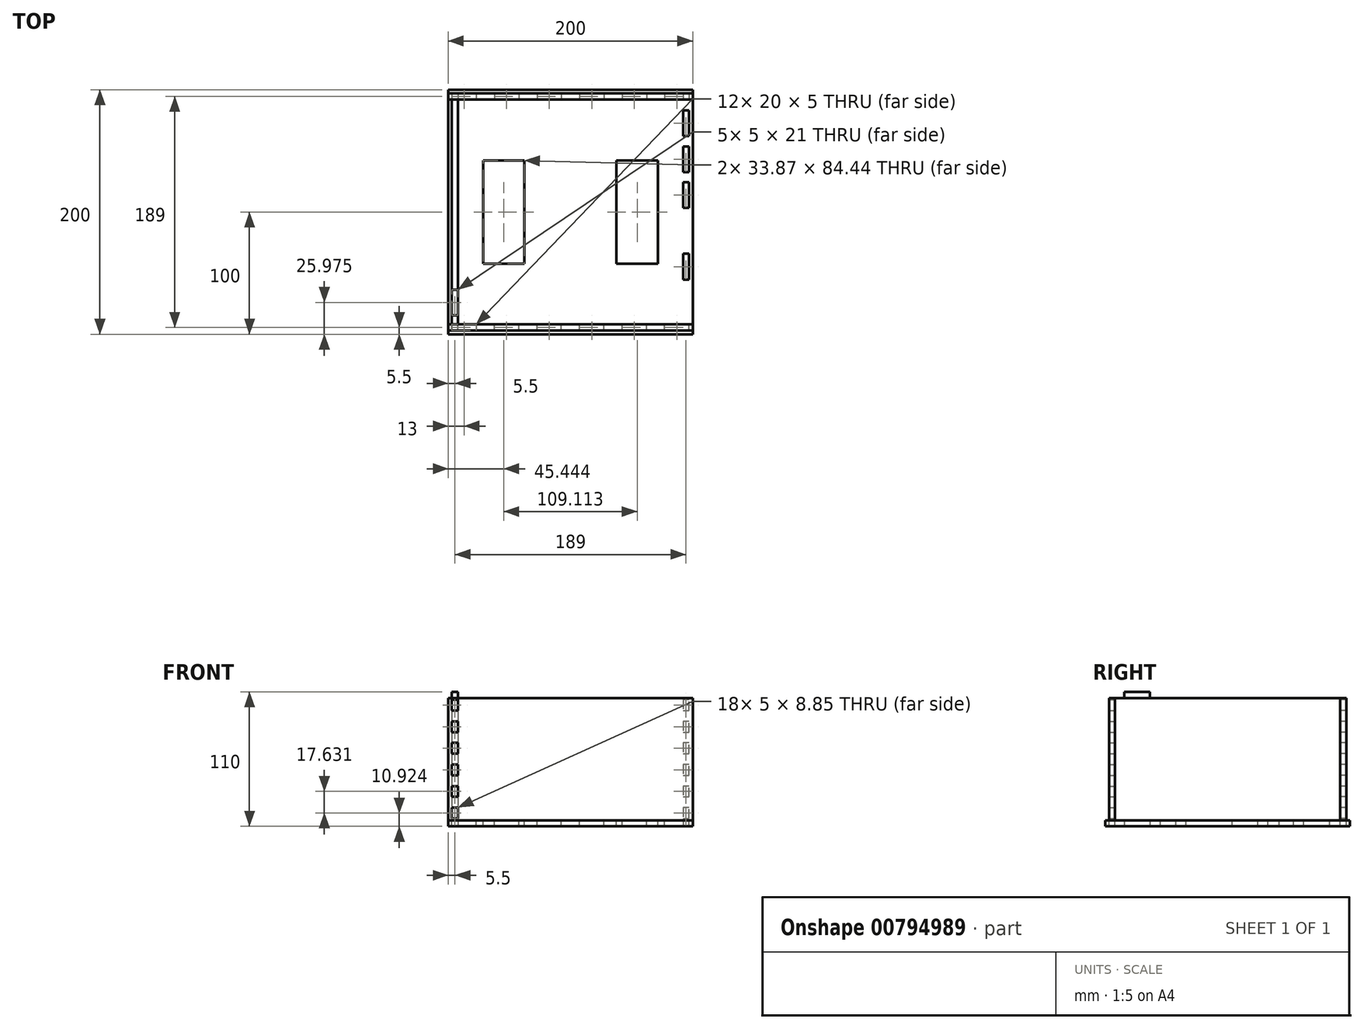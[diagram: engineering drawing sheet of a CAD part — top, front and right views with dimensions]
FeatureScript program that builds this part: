
annotation { "Feature Type Name" : "Feature", "Feature Type Description" : "" }
export const myFeature = defineFeature(function(context is Context, id is Id, definition is map)
    precondition{}
    {
        {
            assignVariable(context, id + "F0", {"name" : "width", "anyValue" : 5});
        }
        {
            var Q0;
            Q0=qCreatedBy(makeId("Top.planeOp"),FACE);
            var sketch = newSketch(context, id + "F1", { "sketchPlane" : qUnion([Q0])});
            skLineSegment(sketch, "E0.bottom", {"start": v(100, -100) * mm, "end": v(-100, -100) * mm});
            skLineSegment(sketch, "E0.top", {"start": v(100, 100) * mm, "end": v(-100, 100) * mm});
            skLineSegment(sketch, "E0.left", {"start": v(100, -100) * mm, "end": v(100, 100) * mm});
            skLineSegment(sketch, "E0.right", {"start": v(-100, -100) * mm, "end": v(-100, 100) * mm});
            skPoint(sketch, "E0.middle", {"position": v(0, 0) * mm});
            skLineSegment(sketch, "E1.0", {"start": v(97, 97) * mm, "end": v(-97, 97) * mm, "construction": true});
            skLineSegment(sketch, "E1.1", {"start": v(97, -97) * mm, "end": v(97, 97) * mm, "construction": true});
            skLineSegment(sketch, "E1.2", {"start": v(97, -97) * mm, "end": v(-97, -97) * mm, "construction": true});
            skLineSegment(sketch, "E1.3", {"start": v(-97, -97) * mm, "end": v(-97, 97) * mm, "construction": true});
            skSolve(sketch);
        }
        {
            var Q0;
            Q0=qSketchRegion(id+"F1",true);
            extrude(context, id + "F2", {"entities" : qUnion([Q0]), "depth" : (getVariable(context, 'width')) * mm});
        }
        {
            var Q0;
            Q0=makeQuery(id+"F2.opExtrude","CAP_FACE",FACE,{"disambiguationData":[OSD([sQuery(id+"F1.wireOp",EDGE,"E0.bottom"),sQuery(id+"F1.wireOp",EDGE,"E0.top"),sQuery(id+"F1.wireOp",EDGE,"E0.left"),sQuery(id+"F1.wireOp",EDGE,"E0.right")])],"isStart":false});
            var sketch = newSketch(context, id + "F3", { "sketchPlane" : qUnion([Q0])});
            skLineSegment(sketch, "E2.0", {"start": v(97, 97) * mm, "end": v(-97, 97) * mm, "construction": true});
            skLineSegment(sketch, "E2.1", {"start": v(97, -97) * mm, "end": v(97, 97) * mm, "construction": true});
            skLineSegment(sketch, "E2.2", {"start": v(97, -97) * mm, "end": v(-97, -97) * mm, "construction": true});
            skLineSegment(sketch, "E2.3", {"start": v(-97, -97) * mm, "end": v(-97, 97) * mm, "construction": true});
            skLineSegment(sketch, "E3.bottom", {"start": v(-97, 97) * mm, "end": v(-77, 97) * mm, "construction": true});
            skLineSegment(sketch, "E3.left", {"start": v(-97, 97) * mm, "end": v(-97, 92) * mm, "construction": true});
            skLineSegment(sketch, "E4.bottom", {"start": v(-97, 97) * mm, "end": v(-77, 97) * mm});
            skLineSegment(sketch, "E4.top", {"start": v(-97, 92) * mm, "end": v(-77, 92) * mm});
            skLineSegment(sketch, "E4.left", {"start": v(-97, 97) * mm, "end": v(-97, 92) * mm});
            skLineSegment(sketch, "E4.right", {"start": v(-77, 97) * mm, "end": v(-77, 92) * mm});
            skLineSegment(sketch, "E5.1.0.0", {"start": v(-42.2, 97) * mm, "end": v(-42.2, 92) * mm});
            skLineSegment(sketch, "E5.1.0.1", {"start": v(-62.2, 92) * mm, "end": v(-42.2, 92) * mm});
            skLineSegment(sketch, "E5.1.0.2", {"start": v(-62.2, 97) * mm, "end": v(-42.2, 97) * mm});
            skLineSegment(sketch, "E5.1.0.3", {"start": v(-62.2, 97) * mm, "end": v(-62.2, 92) * mm});
            skLineSegment(sketch, "E5.2.0.0", {"start": v(-7.4, 97) * mm, "end": v(-7.4, 92) * mm});
            skLineSegment(sketch, "E5.2.0.1", {"start": v(-27.4, 92) * mm, "end": v(-7.4, 92) * mm});
            skLineSegment(sketch, "E5.2.0.2", {"start": v(-27.4, 97) * mm, "end": v(-7.4, 97) * mm});
            skLineSegment(sketch, "E5.2.0.3", {"start": v(-27.4, 97) * mm, "end": v(-27.4, 92) * mm});
            skLineSegment(sketch, "E5.3.0.0", {"start": v(27.4, 97) * mm, "end": v(27.4, 92) * mm});
            skLineSegment(sketch, "E5.3.0.1", {"start": v(7.4, 92) * mm, "end": v(27.4, 92) * mm});
            skLineSegment(sketch, "E5.3.0.2", {"start": v(7.4, 97) * mm, "end": v(27.4, 97) * mm});
            skLineSegment(sketch, "E5.3.0.3", {"start": v(7.4, 97) * mm, "end": v(7.4, 92) * mm});
            skLineSegment(sketch, "E5.4.0.0", {"start": v(62.2, 97) * mm, "end": v(62.2, 92) * mm});
            skLineSegment(sketch, "E5.4.0.1", {"start": v(42.2, 92) * mm, "end": v(62.2, 92) * mm});
            skLineSegment(sketch, "E5.4.0.2", {"start": v(42.2, 97) * mm, "end": v(62.2, 97) * mm});
            skLineSegment(sketch, "E5.4.0.3", {"start": v(42.2, 97) * mm, "end": v(42.2, 92) * mm});
            skLineSegment(sketch, "E5.5.0.0", {"start": v(97, 97) * mm, "end": v(97, 92) * mm});
            skLineSegment(sketch, "E5.5.0.1", {"start": v(77, 92) * mm, "end": v(97, 92) * mm});
            skLineSegment(sketch, "E5.5.0.2", {"start": v(77, 97) * mm, "end": v(97, 97) * mm});
            skLineSegment(sketch, "E5.5.0.3", {"start": v(77, 97) * mm, "end": v(77, 92) * mm});
            skLineSegment(sketch, "E5.direction1", {"start": v(-77, 92) * mm, "end": v(-42.2, 92) * mm, "construction": true});
            skLineSegment(sketch, "E6.MirrorCS", {"start": v(-97, -97) * mm, "end": v(-97, -92) * mm});
            skLineSegment(sketch, "E7.MirrorCS", {"start": v(-77, -97) * mm, "end": v(-77, -92) * mm});
            skLineSegment(sketch, "E8.MirrorCS", {"start": v(-97, -97) * mm, "end": v(-97, -92) * mm, "construction": true});
            skLineSegment(sketch, "E9.MirrorCS", {"start": v(97, -97) * mm, "end": v(97, -92) * mm});
            skLineSegment(sketch, "E10.MirrorCS", {"start": v(77, -97) * mm, "end": v(77, -92) * mm});
            skLineSegment(sketch, "E11.MirrorCS", {"start": v(-42.2, -97) * mm, "end": v(-42.2, -92) * mm});
            skLineSegment(sketch, "E12.MirrorCS", {"start": v(62.2, -97) * mm, "end": v(62.2, -92) * mm});
            skLineSegment(sketch, "E13.MirrorCS", {"start": v(-62.2, -97) * mm, "end": v(-62.2, -92) * mm});
            skLineSegment(sketch, "E14.MirrorCS", {"start": v(-7.4, -97) * mm, "end": v(-7.4, -92) * mm});
            skLineSegment(sketch, "E15.MirrorCS", {"start": v(-27.4, -97) * mm, "end": v(-27.4, -92) * mm});
            skLineSegment(sketch, "E16.MirrorCS", {"start": v(7.4, -97) * mm, "end": v(7.4, -92) * mm});
            skLineSegment(sketch, "E17.MirrorCS", {"start": v(27.4, -97) * mm, "end": v(27.4, -92) * mm});
            skLineSegment(sketch, "E18.MirrorCS", {"start": v(42.2, -97) * mm, "end": v(42.2, -92) * mm});
            skLineSegment(sketch, "E19.MirrorCS", {"start": v(-62.2, -92) * mm, "end": v(-42.2, -92) * mm});
            skLineSegment(sketch, "E20.MirrorCS", {"start": v(-27.4, -97) * mm, "end": v(-7.4, -97) * mm});
            skLineSegment(sketch, "E21.MirrorCS", {"start": v(7.4, -97) * mm, "end": v(27.4, -97) * mm});
            skLineSegment(sketch, "E22.MirrorCS", {"start": v(42.2, -97) * mm, "end": v(62.2, -97) * mm});
            skLineSegment(sketch, "E23.MirrorCS", {"start": v(77, -97) * mm, "end": v(97, -97) * mm});
            skLineSegment(sketch, "E24.MirrorCS", {"start": v(-62.2, -97) * mm, "end": v(-42.2, -97) * mm});
            skLineSegment(sketch, "E25.MirrorCS", {"start": v(-97, -97) * mm, "end": v(-77, -97) * mm});
            skLineSegment(sketch, "E26.MirrorCS", {"start": v(42.2, -92) * mm, "end": v(62.2, -92) * mm});
            skLineSegment(sketch, "E27.MirrorCS", {"start": v(77, -92) * mm, "end": v(97, -92) * mm});
            skLineSegment(sketch, "E28.MirrorCS", {"start": v(-77, -92) * mm, "end": v(-42.2, -92) * mm, "construction": true});
            skLineSegment(sketch, "E29.MirrorCS", {"start": v(-27.4, -92) * mm, "end": v(-7.4, -92) * mm});
            skLineSegment(sketch, "E30.MirrorCS", {"start": v(-97, -97) * mm, "end": v(-77, -97) * mm, "construction": true});
            skLineSegment(sketch, "E31.MirrorCS", {"start": v(-97, -92) * mm, "end": v(-77, -92) * mm});
            skLineSegment(sketch, "E32.MirrorCS", {"start": v(7.4, -92) * mm, "end": v(27.4, -92) * mm});
            skSolve(sketch);
        }
        {
            var Q0;
            Q0=qSketchRegion(id+"F3",true);
            extrude(context, id + "F4", {"entities" : qUnion([Q0]), "operationType" : NewBodyOperationType.REMOVE, "oppositeDirection" : true, "depth" : 25 * mm});
        }
        {
            var Q0;
            Q0=makeQuery(id+"F2.opExtrude","CAP_FACE",FACE,{"disambiguationData":[OSD([sQuery(id+"F1.wireOp",EDGE,"E0.bottom"),sQuery(id+"F1.wireOp",EDGE,"E0.top"),sQuery(id+"F1.wireOp",EDGE,"E0.left"),sQuery(id+"F1.wireOp",EDGE,"E0.right")])],"isStart":false});
            var sketch = newSketch(context, id + "F5", { "sketchPlane" : qUnion([Q0])});
            skLineSegment(sketch, "E33.0", {"start": v(-97, 97) * mm, "end": v(-77, 97) * mm});
            skSolve(sketch);
        }
        {
            var Q0;
            Q0=makeQuery(id+"F5.imprint","IMPRINT",FACE,{"disambiguationData":[TD([[makeQuery(id+"F5.imprint","IMPRINT",EDGE,{"derivedFrom":makeQuery(id+"F4.boolean.opBoolean","COPY",EDGE,{"derivedFrom":makeQuery(id+"F4.opExtrude","CAP_EDGE",EDGE,{"disambiguationData":[OSD([sQuery(id+"F3.wireOp",EDGE,"E5.1.0.0")])],"isStart":true})})}),-1.0]])]});
            var Q1;
            Q1=makeQuery(id+"F5.imprint","IMPRINT",FACE,{"disambiguationData":[TD([[makeQuery(id+"F5.imprint","IMPRINT",EDGE,{"derivedFrom":sQuery(id+"F5.wireOp",EDGE,"E33.0")}),-1.0]])]});
            var Q2;
            Q2=makeQuery(id+"F5.imprint","IMPRINT",FACE,{"disambiguationData":[TD([[makeQuery(id+"F5.imprint","IMPRINT",EDGE,{"derivedFrom":makeQuery(id+"F4.boolean.opBoolean","COPY",EDGE,{"derivedFrom":makeQuery(id+"F4.opExtrude","CAP_EDGE",EDGE,{"disambiguationData":[OSD([sQuery(id+"F3.wireOp",EDGE,"E5.2.0.0")])],"isStart":true})})}),-1.0]])]});
            var Q3;
            Q3=makeQuery(id+"F5.imprint","IMPRINT",FACE,{"disambiguationData":[TD([[makeQuery(id+"F5.imprint","IMPRINT",EDGE,{"derivedFrom":makeQuery(id+"F4.boolean.opBoolean","COPY",EDGE,{"derivedFrom":makeQuery(id+"F4.opExtrude","CAP_EDGE",EDGE,{"disambiguationData":[OSD([sQuery(id+"F3.wireOp",EDGE,"E5.3.0.0")])],"isStart":true})})}),-1.0]])]});
            var Q4;
            Q4=makeQuery(id+"F5.imprint","IMPRINT",FACE,{"disambiguationData":[TD([[makeQuery(id+"F5.imprint","IMPRINT",EDGE,{"derivedFrom":makeQuery(id+"F4.boolean.opBoolean","COPY",EDGE,{"derivedFrom":makeQuery(id+"F4.opExtrude","CAP_EDGE",EDGE,{"disambiguationData":[OSD([sQuery(id+"F3.wireOp",EDGE,"E5.4.0.0")])],"isStart":true})})}),-1.0]])]});
            var Q5;
            Q5=makeQuery(id+"F5.imprint","IMPRINT",FACE,{"disambiguationData":[TD([[makeQuery(id+"F5.imprint","IMPRINT",EDGE,{"derivedFrom":makeQuery(id+"F4.boolean.opBoolean","COPY",EDGE,{"derivedFrom":makeQuery(id+"F4.opExtrude","CAP_EDGE",EDGE,{"disambiguationData":[OSD([sQuery(id+"F3.wireOp",EDGE,"E5.5.0.0")])],"isStart":true})})}),-1.0]])]});
            var Q6;
            Q6=makeQuery(id+"F2.opExtrude","CAP_FACE",FACE,{"disambiguationData":[OSD([sQuery(id+"F1.wireOp",EDGE,"E0.bottom"),sQuery(id+"F1.wireOp",EDGE,"E0.top"),sQuery(id+"F1.wireOp",EDGE,"E0.left"),sQuery(id+"F1.wireOp",EDGE,"E0.right")])],"isStart":true});
            extrude(context, id + "F6", {"entities" : qUnion([Q0, Q1, Q2, Q3, Q4, Q5]), "endBound" : BoundingType.UP_TO_SURFACE, "oppositeDirection" : true, "endBoundEntityFace" : qUnion([Q6]), "depth" : 25 * mm});
        }
        {
            var Q0;
            Q0=makeQuery(id+"F2.opExtrude","CAP_FACE",FACE,{"disambiguationData":[OSD([sQuery(id+"F1.wireOp",EDGE,"E0.bottom"),sQuery(id+"F1.wireOp",EDGE,"E0.top"),sQuery(id+"F1.wireOp",EDGE,"E0.left"),sQuery(id+"F1.wireOp",EDGE,"E0.right")])],"isStart":false});
            var sketch = newSketch(context, id + "F7", { "sketchPlane" : qUnion([Q0])});
            skLineSegment(sketch, "E34.bottom", {"start": v(-100, 97) * mm, "end": v(100, 97) * mm});
            skLineSegment(sketch, "E34.top", {"start": v(-100, 92) * mm, "end": v(100, 92) * mm});
            skLineSegment(sketch, "E34.left", {"start": v(-100, 97) * mm, "end": v(-100, 92) * mm});
            skLineSegment(sketch, "E34.right", {"start": v(100, 97) * mm, "end": v(100, 92) * mm});
            skSolve(sketch);
        }
        {
            var Q0;
            Q0=qSketchRegion(id+"F7",true);
            extrude(context, id + "F8", {"entities" : qUnion([Q0]), "depth" : 100 * mm});
        }
        {
            var Q0;
            Q0=makeQuery(id+"F2.opExtrude","CAP_FACE",FACE,{"disambiguationData":[OSD([sQuery(id+"F1.wireOp",EDGE,"E0.bottom"),sQuery(id+"F1.wireOp",EDGE,"E0.top"),sQuery(id+"F1.wireOp",EDGE,"E0.left"),sQuery(id+"F1.wireOp",EDGE,"E0.right")])],"isStart":true});
            var sketch = newSketch(context, id + "F9", { "sketchPlane" : qUnion([Q0])});
            skLineSegment(sketch, "E35.0", {"start": v(97, 97) * mm, "end": v(97, -97) * mm});
            skLineSegment(sketch, "E35.1", {"start": v(97, 97) * mm, "end": v(-97, 97) * mm});
            skLineSegment(sketch, "E35.2", {"start": v(-97, 97) * mm, "end": v(-97, -97) * mm});
            skLineSegment(sketch, "E35.3", {"start": v(97, -97) * mm, "end": v(-97, -97) * mm});
            skLineSegment(sketch, "E36.bottom", {"start": v(-97, 84.52) * mm, "end": v(-92, 84.52) * mm});
            skLineSegment(sketch, "E36.top", {"start": v(-97, 63.52) * mm, "end": v(-92, 63.52) * mm});
            skLineSegment(sketch, "E36.left", {"start": v(-97, 84.52) * mm, "end": v(-97, 63.52) * mm});
            skLineSegment(sketch, "E36.right", {"start": v(-92, 84.52) * mm, "end": v(-92, 63.52) * mm});
            skLineSegment(sketch, "E37.1.0.0", {"start": v(-97, 55.22) * mm, "end": v(-97, 34.22) * mm});
            skLineSegment(sketch, "E37.1.0.1", {"start": v(-97, 55.22) * mm, "end": v(-92, 55.22) * mm});
            skLineSegment(sketch, "E37.1.0.2", {"start": v(-97, 34.22) * mm, "end": v(-92, 34.22) * mm});
            skLineSegment(sketch, "E37.1.0.3", {"start": v(-92, 55.22) * mm, "end": v(-92, 34.22) * mm});
            skLineSegment(sketch, "E37.2.0.0", {"start": v(-97, 25.91) * mm, "end": v(-97, 4.91) * mm});
            skLineSegment(sketch, "E37.2.0.1", {"start": v(-97, 25.91) * mm, "end": v(-92, 25.91) * mm});
            skLineSegment(sketch, "E37.2.0.2", {"start": v(-97, 4.91) * mm, "end": v(-92, 4.91) * mm});
            skLineSegment(sketch, "E37.2.0.3", {"start": v(-92, 25.91) * mm, "end": v(-92, 4.91) * mm});
            skLineSegment(sketch, "E37.3.0.0", {"start": v(-97, -3.4) * mm, "end": v(-97, -24.4) * mm});
            skLineSegment(sketch, "E37.3.0.1", {"start": v(-97, -3.4) * mm, "end": v(-92, -3.4) * mm});
            skLineSegment(sketch, "E37.3.0.2", {"start": v(-97, -24.4) * mm, "end": v(-92, -24.4) * mm});
            skLineSegment(sketch, "E37.3.0.3", {"start": v(-92, -3.4) * mm, "end": v(-92, -24.4) * mm});
            skLineSegment(sketch, "E37.4.0.0", {"start": v(-97, -32.7) * mm, "end": v(-97, -53.7) * mm});
            skLineSegment(sketch, "E37.4.0.1", {"start": v(-97, -32.7) * mm, "end": v(-92, -32.7) * mm});
            skLineSegment(sketch, "E37.4.0.2", {"start": v(-97, -53.7) * mm, "end": v(-92, -53.7) * mm});
            skLineSegment(sketch, "E37.4.0.3", {"start": v(-92, -32.7) * mm, "end": v(-92, -53.7) * mm});
            skLineSegment(sketch, "E37.5.0.0", {"start": v(-97, -62) * mm, "end": v(-97, -83) * mm});
            skLineSegment(sketch, "E37.5.0.1", {"start": v(-97, -62) * mm, "end": v(-92, -62) * mm});
            skLineSegment(sketch, "E37.5.0.2", {"start": v(-97, -83) * mm, "end": v(-92, -83) * mm});
            skLineSegment(sketch, "E37.5.0.3", {"start": v(-92, -62) * mm, "end": v(-92, -83) * mm});
            skLineSegment(sketch, "E37.direction1", {"start": v(-97, 63.52) * mm, "end": v(-97, 34.22) * mm, "construction": true});
            skLineSegment(sketch, "E38.MirrorCS", {"start": v(97, 84.52) * mm, "end": v(97, 63.52) * mm});
            skLineSegment(sketch, "E39.MirrorCS", {"start": v(97, 84.52) * mm, "end": v(92, 84.52) * mm});
            skLineSegment(sketch, "E40.MirrorCS", {"start": v(92, 84.52) * mm, "end": v(92, 63.52) * mm});
            skLineSegment(sketch, "E41.MirrorCS", {"start": v(97, 63.52) * mm, "end": v(92, 63.52) * mm});
            skLineSegment(sketch, "E42.MirrorCS", {"start": v(97, 55.22) * mm, "end": v(92, 55.22) * mm});
            skLineSegment(sketch, "E43.MirrorCS", {"start": v(92, 55.22) * mm, "end": v(92, 34.22) * mm});
            skLineSegment(sketch, "E44.MirrorCS", {"start": v(97, 63.52) * mm, "end": v(97, 34.22) * mm, "construction": true});
            skLineSegment(sketch, "E45.MirrorCS", {"start": v(97, 55.22) * mm, "end": v(97, 34.22) * mm});
            skLineSegment(sketch, "E46.MirrorCS", {"start": v(97, 25.91) * mm, "end": v(97, 4.91) * mm});
            skLineSegment(sketch, "E47.MirrorCS", {"start": v(97, 34.22) * mm, "end": v(92, 34.22) * mm});
            skLineSegment(sketch, "E48.MirrorCS", {"start": v(97, 25.91) * mm, "end": v(92, 25.91) * mm});
            skLineSegment(sketch, "E49.MirrorCS", {"start": v(92, 25.91) * mm, "end": v(92, 4.91) * mm});
            skLineSegment(sketch, "E50.MirrorCS", {"start": v(97, 4.91) * mm, "end": v(92, 4.91) * mm});
            skLineSegment(sketch, "E51.MirrorCS", {"start": v(97, -32.7) * mm, "end": v(92, -32.7) * mm});
            skLineSegment(sketch, "E52.MirrorCS", {"start": v(92, -32.7) * mm, "end": v(92, -53.7) * mm});
            skLineSegment(sketch, "E53.MirrorCS", {"start": v(97, -32.7) * mm, "end": v(97, -53.7) * mm});
            skLineSegment(sketch, "E54.MirrorCS", {"start": v(97, -53.7) * mm, "end": v(92, -53.7) * mm});
            skLineSegment(sketch, "E55.MirrorCS", {"start": v(97, -62) * mm, "end": v(92, -62) * mm});
            skLineSegment(sketch, "E56.MirrorCS", {"start": v(92, -62) * mm, "end": v(92, -83) * mm});
            skLineSegment(sketch, "E57.MirrorCS", {"start": v(97, -62) * mm, "end": v(97, -83) * mm});
            skLineSegment(sketch, "E58.MirrorCS", {"start": v(97, -83) * mm, "end": v(92, -83) * mm});
            skLineSegment(sketch, "E59.MirrorCS", {"start": v(92, -3.4) * mm, "end": v(92, -24.4) * mm});
            skLineSegment(sketch, "E60.MirrorCS", {"start": v(97, -3.4) * mm, "end": v(92, -3.4) * mm});
            skLineSegment(sketch, "E61.MirrorCS", {"start": v(97, -24.4) * mm, "end": v(92, -24.4) * mm});
            skLineSegment(sketch, "E62.MirrorCS", {"start": v(97, -3.4) * mm, "end": v(97, -24.4) * mm});
            skSolve(sketch);
        }
        {
            var Q0;
            Q0=makeQuery(id+"F9.imprint","IMPRINT",FACE,{"disambiguationData":[TD([[makeQuery(id+"F9.imprint","IMPRINT",EDGE,{"derivedFrom":sQuery(id+"F9.wireOp",EDGE,"E38.MirrorCS")}),-1.0]])]});
            var Q1;
            Q1=makeQuery(id+"F9.imprint","IMPRINT",FACE,{"disambiguationData":[TD([[makeQuery(id+"F9.imprint","IMPRINT",EDGE,{"derivedFrom":sQuery(id+"F9.wireOp",EDGE,"E42.MirrorCS")}),1.0]])]});
            var Q2;
            Q2=makeQuery(id+"F9.imprint","IMPRINT",FACE,{"disambiguationData":[TD([[makeQuery(id+"F9.imprint","IMPRINT",EDGE,{"derivedFrom":sQuery(id+"F9.wireOp",EDGE,"E46.MirrorCS")}),-1.0]])]});
            var Q3;
            Q3=makeQuery(id+"F9.imprint","IMPRINT",FACE,{"disambiguationData":[TD([[makeQuery(id+"F9.imprint","IMPRINT",EDGE,{"derivedFrom":sQuery(id+"F9.wireOp",EDGE,"E59.MirrorCS")}),1.0]])]});
            var Q4;
            Q4=makeQuery(id+"F9.imprint","IMPRINT",FACE,{"disambiguationData":[TD([[makeQuery(id+"F9.imprint","IMPRINT",EDGE,{"derivedFrom":sQuery(id+"F9.wireOp",EDGE,"E51.MirrorCS")}),1.0]])]});
            var Q5;
            Q5=makeQuery(id+"F9.imprint","IMPRINT",FACE,{"disambiguationData":[TD([[makeQuery(id+"F9.imprint","IMPRINT",EDGE,{"derivedFrom":sQuery(id+"F9.wireOp",EDGE,"E55.MirrorCS")}),1.0]])]});
            var Q6;
            Q6=makeQuery(id+"F9.imprint","IMPRINT",FACE,{"disambiguationData":[TD([[makeQuery(id+"F9.imprint","IMPRINT",EDGE,{"derivedFrom":sQuery(id+"F9.wireOp",EDGE,"E36.bottom")}),-1.0]])]});
            var Q7;
            Q7=makeQuery(id+"F9.imprint","IMPRINT",FACE,{"disambiguationData":[TD([[makeQuery(id+"F9.imprint","IMPRINT",EDGE,{"derivedFrom":sQuery(id+"F9.wireOp",EDGE,"E37.1.0.0")}),1.0]])]});
            var Q8;
            Q8=makeQuery(id+"F9.imprint","IMPRINT",FACE,{"disambiguationData":[TD([[makeQuery(id+"F9.imprint","IMPRINT",EDGE,{"derivedFrom":sQuery(id+"F9.wireOp",EDGE,"E37.2.0.0")}),1.0]])]});
            var Q9;
            Q9=makeQuery(id+"F9.imprint","IMPRINT",FACE,{"disambiguationData":[TD([[makeQuery(id+"F9.imprint","IMPRINT",EDGE,{"derivedFrom":sQuery(id+"F9.wireOp",EDGE,"E37.3.0.0")}),1.0]])]});
            var Q10;
            Q10=makeQuery(id+"F9.imprint","IMPRINT",FACE,{"disambiguationData":[TD([[makeQuery(id+"F9.imprint","IMPRINT",EDGE,{"derivedFrom":sQuery(id+"F9.wireOp",EDGE,"E37.4.0.0")}),1.0]])]});
            var Q11;
            Q11=makeQuery(id+"F9.imprint","IMPRINT",FACE,{"disambiguationData":[TD([[makeQuery(id+"F9.imprint","IMPRINT",EDGE,{"derivedFrom":sQuery(id+"F9.wireOp",EDGE,"E37.5.0.0")}),1.0]])]});
            extrude(context, id + "F10", {"entities" : qUnion([Q0, Q1, Q2, Q3, Q4, Q5, Q6, Q7, Q8, Q9, Q10, Q11]), "operationType" : NewBodyOperationType.REMOVE, "oppositeDirection" : true, "depth" : 25 * mm});
        }
        {
            var Q0;
            Q0=makeQuery(id+"F8.opExtrude","SWEPT_BODY",BODY,{"disambiguationData":[OSD([sQuery(id+"F7.wireOp",EDGE,"E34.bottom"),sQuery(id+"F7.wireOp",EDGE,"E34.top"),sQuery(id+"F7.wireOp",EDGE,"E34.left"),sQuery(id+"F7.wireOp",EDGE,"E34.right")])]});
            var Q1;
            Q1=makeQuery(id+"F6.opExtrude","SWEPT_BODY",BODY,{"disambiguationData":[OSD([sQuery(id+"F3.wireOp",EDGE,"E5.5.0.0"),sQuery(id+"F3.wireOp",EDGE,"E5.5.0.1"),sQuery(id+"F3.wireOp",EDGE,"E5.5.0.2"),sQuery(id+"F3.wireOp",EDGE,"E5.5.0.3")])]});
            var Q2;
            Q2=makeQuery(id+"F6.opExtrude","SWEPT_BODY",BODY,{"disambiguationData":[OSD([sQuery(id+"F3.wireOp",EDGE,"E5.4.0.0"),sQuery(id+"F3.wireOp",EDGE,"E5.4.0.1"),sQuery(id+"F3.wireOp",EDGE,"E5.4.0.2"),sQuery(id+"F3.wireOp",EDGE,"E5.4.0.3")])]});
            var Q3;
            Q3=makeQuery(id+"F6.opExtrude","SWEPT_BODY",BODY,{"disambiguationData":[OSD([sQuery(id+"F3.wireOp",EDGE,"E5.3.0.0"),sQuery(id+"F3.wireOp",EDGE,"E5.3.0.1"),sQuery(id+"F3.wireOp",EDGE,"E5.3.0.2"),sQuery(id+"F3.wireOp",EDGE,"E5.3.0.3")])]});
            var Q4;
            Q4=makeQuery(id+"F6.opExtrude","SWEPT_BODY",BODY,{"disambiguationData":[OSD([sQuery(id+"F3.wireOp",EDGE,"E5.2.0.0"),sQuery(id+"F3.wireOp",EDGE,"E5.2.0.1"),sQuery(id+"F3.wireOp",EDGE,"E5.2.0.2"),sQuery(id+"F3.wireOp",EDGE,"E5.2.0.3")])]});
            var Q5;
            Q5=makeQuery(id+"F6.opExtrude","SWEPT_BODY",BODY,{"disambiguationData":[OSD([sQuery(id+"F3.wireOp",EDGE,"E5.1.0.0"),sQuery(id+"F3.wireOp",EDGE,"E5.1.0.1"),sQuery(id+"F3.wireOp",EDGE,"E5.1.0.2"),sQuery(id+"F3.wireOp",EDGE,"E5.1.0.3")])]});
            var Q6;
            Q6=makeQuery(id+"F6.opExtrude","SWEPT_BODY",BODY,{"disambiguationData":[OSD([sQuery(id+"F3.wireOp",EDGE,"E4.top"),sQuery(id+"F3.wireOp",EDGE,"E4.left"),sQuery(id+"F3.wireOp",EDGE,"E4.right"),sQuery(id+"F5.wireOp",EDGE,"E33.0")])]});
            booleanBodies(context, id + "F11", {"operationType" : BooleanOperationType.UNION, "tools" : qUnion([Q0, Q1, Q2, Q3, Q4, Q5, Q6])});
        }
        {
            var Q0;
            Q0=makeQuery(id+"F11.opBoolean","MERGE",FACE,{"derivedFrom":[makeQuery(id+"F6.opExtrude","SWEPT_FACE",FACE,{"disambiguationData":[OSD([sQuery(id+"F3.wireOp",EDGE,"E4.top")])]}),makeQuery(id+"F6.opExtrude","SWEPT_FACE",FACE,{"disambiguationData":[OSD([sQuery(id+"F3.wireOp",EDGE,"E5.1.0.1")])]}),makeQuery(id+"F6.opExtrude","SWEPT_FACE",FACE,{"disambiguationData":[OSD([sQuery(id+"F3.wireOp",EDGE,"E5.2.0.1")])]}),makeQuery(id+"F6.opExtrude","SWEPT_FACE",FACE,{"disambiguationData":[OSD([sQuery(id+"F3.wireOp",EDGE,"E5.3.0.1")])]}),makeQuery(id+"F6.opExtrude","SWEPT_FACE",FACE,{"disambiguationData":[OSD([sQuery(id+"F3.wireOp",EDGE,"E5.4.0.1")])]}),makeQuery(id+"F6.opExtrude","SWEPT_FACE",FACE,{"disambiguationData":[OSD([sQuery(id+"F3.wireOp",EDGE,"E5.5.0.1")])]}),makeQuery(id+"F8.opExtrude","SWEPT_FACE",FACE,{"disambiguationData":[OSD([sQuery(id+"F7.wireOp",EDGE,"E34.top")])]})]});
            var sketch = newSketch(context, id + "F12", { "sketchPlane" : qUnion([Q0])});
            skLineSegment(sketch, "E63.bottom", {"start": v(-100, 105) * mm, "end": v(100, 105) * mm});
            skLineSegment(sketch, "E63.top", {"start": v(-100, 5) * mm, "end": v(100, 5) * mm});
            skLineSegment(sketch, "E63.left", {"start": v(-100, 105) * mm, "end": v(-100, 5) * mm});
            skLineSegment(sketch, "E63.right", {"start": v(100, 105) * mm, "end": v(100, 5) * mm});
            skLineSegment(sketch, "E64.bottom", {"start": v(-147, 8) * mm, "end": v(-142, 8) * mm});
            skLineSegment(sketch, "E64.top", {"start": v(-147, 18) * mm, "end": v(-142, 18) * mm});
            skLineSegment(sketch, "E64.left", {"start": v(-147, 8) * mm, "end": v(-147, 18) * mm});
            skLineSegment(sketch, "E64.right", {"start": v(-142, 8) * mm, "end": v(-142, 18) * mm});
            skLineSegment(sketch, "E65.1.0.0", {"start": v(-142, 24.8) * mm, "end": v(-142, 34.8) * mm});
            skLineSegment(sketch, "E65.1.0.1", {"start": v(-147, 34.8) * mm, "end": v(-142, 34.8) * mm});
            skLineSegment(sketch, "E65.1.0.2", {"start": v(-147, 24.8) * mm, "end": v(-147, 34.8) * mm});
            skLineSegment(sketch, "E65.1.0.3", {"start": v(-147, 24.8) * mm, "end": v(-142, 24.8) * mm});
            skLineSegment(sketch, "E65.2.0.0", {"start": v(-142, 41.6) * mm, "end": v(-142, 51.6) * mm});
            skLineSegment(sketch, "E65.2.0.1", {"start": v(-147, 51.6) * mm, "end": v(-142, 51.6) * mm});
            skLineSegment(sketch, "E65.2.0.2", {"start": v(-147, 41.6) * mm, "end": v(-147, 51.6) * mm});
            skLineSegment(sketch, "E65.2.0.3", {"start": v(-147, 41.6) * mm, "end": v(-142, 41.6) * mm});
            skLineSegment(sketch, "E65.3.0.0", {"start": v(-142, 58.4) * mm, "end": v(-142, 68.4) * mm});
            skLineSegment(sketch, "E65.3.0.1", {"start": v(-147, 68.4) * mm, "end": v(-142, 68.4) * mm});
            skLineSegment(sketch, "E65.3.0.2", {"start": v(-147, 58.4) * mm, "end": v(-147, 68.4) * mm});
            skLineSegment(sketch, "E65.3.0.3", {"start": v(-147, 58.4) * mm, "end": v(-142, 58.4) * mm});
            skLineSegment(sketch, "E65.4.0.0", {"start": v(-142, 75.2) * mm, "end": v(-142, 85.2) * mm});
            skLineSegment(sketch, "E65.4.0.1", {"start": v(-147, 85.2) * mm, "end": v(-142, 85.2) * mm});
            skLineSegment(sketch, "E65.4.0.2", {"start": v(-147, 75.2) * mm, "end": v(-147, 85.2) * mm});
            skLineSegment(sketch, "E65.4.0.3", {"start": v(-147, 75.2) * mm, "end": v(-142, 75.2) * mm});
            skLineSegment(sketch, "E65.5.0.0", {"start": v(-142, 92) * mm, "end": v(-142, 102) * mm});
            skLineSegment(sketch, "E65.5.0.1", {"start": v(-147, 102) * mm, "end": v(-142, 102) * mm});
            skLineSegment(sketch, "E65.5.0.2", {"start": v(-147, 92) * mm, "end": v(-147, 102) * mm});
            skLineSegment(sketch, "E65.5.0.3", {"start": v(-147, 92) * mm, "end": v(-142, 92) * mm});
            skLineSegment(sketch, "E65.direction1", {"start": v(-142, 8) * mm, "end": v(-142, 24.8) * mm, "construction": true});
            skLineSegment(sketch, "E66.MirrorCS", {"start": v(142, 92) * mm, "end": v(142, 102) * mm});
            skLineSegment(sketch, "E67.MirrorCS", {"start": v(147, 102) * mm, "end": v(142, 102) * mm});
            skLineSegment(sketch, "E68.MirrorCS", {"start": v(147, 92) * mm, "end": v(147, 102) * mm});
            skLineSegment(sketch, "E69.MirrorCS", {"start": v(147, 92) * mm, "end": v(142, 92) * mm});
            skLineSegment(sketch, "E70.MirrorCS", {"start": v(147, 51.6) * mm, "end": v(142, 51.6) * mm});
            skLineSegment(sketch, "E71.MirrorCS", {"start": v(147, 58.4) * mm, "end": v(142, 58.4) * mm});
            skLineSegment(sketch, "E72.MirrorCS", {"start": v(147, 75.2) * mm, "end": v(142, 75.2) * mm});
            skLineSegment(sketch, "E73.MirrorCS", {"start": v(147, 41.6) * mm, "end": v(142, 41.6) * mm});
            skLineSegment(sketch, "E74.MirrorCS", {"start": v(147, 18) * mm, "end": v(142, 18) * mm});
            skLineSegment(sketch, "E75.MirrorCS", {"start": v(147, 68.4) * mm, "end": v(142, 68.4) * mm});
            skLineSegment(sketch, "E76.MirrorCS", {"start": v(147, 85.2) * mm, "end": v(142, 85.2) * mm});
            skLineSegment(sketch, "E77.MirrorCS", {"start": v(147, 24.8) * mm, "end": v(142, 24.8) * mm});
            skLineSegment(sketch, "E78.MirrorCS", {"start": v(142, 75.2) * mm, "end": v(142, 85.2) * mm});
            skLineSegment(sketch, "E79.MirrorCS", {"start": v(147, 41.6) * mm, "end": v(147, 51.6) * mm});
            skLineSegment(sketch, "E80.MirrorCS", {"start": v(100, 5) * mm, "end": v(-100, 5) * mm});
            skLineSegment(sketch, "E81.MirrorCS", {"start": v(147, 8) * mm, "end": v(142, 8) * mm});
            skLineSegment(sketch, "E82.MirrorCS", {"start": v(147, 8) * mm, "end": v(147, 18) * mm});
            skLineSegment(sketch, "E83.MirrorCS", {"start": v(142, 8) * mm, "end": v(142, 24.8) * mm, "construction": true});
            skLineSegment(sketch, "E84.MirrorCS", {"start": v(142, 24.8) * mm, "end": v(142, 34.8) * mm});
            skLineSegment(sketch, "E85.MirrorCS", {"start": v(147, 34.8) * mm, "end": v(142, 34.8) * mm});
            skLineSegment(sketch, "E86.MirrorCS", {"start": v(147, 24.8) * mm, "end": v(147, 34.8) * mm});
            skLineSegment(sketch, "E87.MirrorCS", {"start": v(142, 41.6) * mm, "end": v(142, 51.6) * mm});
            skLineSegment(sketch, "E88.MirrorCS", {"start": v(142, 58.4) * mm, "end": v(142, 68.4) * mm});
            skLineSegment(sketch, "E89.MirrorCS", {"start": v(147, 58.4) * mm, "end": v(147, 68.4) * mm});
            skLineSegment(sketch, "E90.MirrorCS", {"start": v(147, 75.2) * mm, "end": v(147, 85.2) * mm});
            skLineSegment(sketch, "E91", {"start": v(142, 18) * mm, "end": v(142, 8) * mm});
            skSolve(sketch);
        }
        {
            var Q0;
            Q0=makeQuery(id+"F12.imprint","IMPRINT",FACE,{"disambiguationData":[TD([[makeQuery(id+"F12.imprint","IMPRINT",EDGE,{"derivedFrom":sQuery(id+"F12.wireOp",EDGE,"E65.5.0.0")}),1.0]])]});
            var Q1;
            Q1=makeQuery(id+"F12.imprint","IMPRINT",FACE,{"disambiguationData":[TD([[makeQuery(id+"F12.imprint","IMPRINT",EDGE,{"derivedFrom":sQuery(id+"F12.wireOp",EDGE,"E65.4.0.0")}),1.0]])]});
            var Q2;
            Q2=makeQuery(id+"F12.imprint","IMPRINT",FACE,{"disambiguationData":[TD([[makeQuery(id+"F12.imprint","IMPRINT",EDGE,{"derivedFrom":sQuery(id+"F12.wireOp",EDGE,"E65.3.0.0")}),1.0]])]});
            var Q3;
            Q3=makeQuery(id+"F12.imprint","IMPRINT",FACE,{"disambiguationData":[TD([[makeQuery(id+"F12.imprint","IMPRINT",EDGE,{"derivedFrom":sQuery(id+"F12.wireOp",EDGE,"E65.2.0.0")}),1.0]])]});
            var Q4;
            Q4=makeQuery(id+"F12.imprint","IMPRINT",FACE,{"disambiguationData":[TD([[makeQuery(id+"F12.imprint","IMPRINT",EDGE,{"derivedFrom":sQuery(id+"F12.wireOp",EDGE,"E65.1.0.0")}),1.0]])]});
            var Q5;
            Q5=makeQuery(id+"F12.imprint","IMPRINT",FACE,{"disambiguationData":[TD([[makeQuery(id+"F12.imprint","IMPRINT",EDGE,{"derivedFrom":sQuery(id+"F12.wireOp",EDGE,"E64.bottom")}),1.0]])]});
            var Q6;
            Q6=makeQuery(id+"F12.imprint","IMPRINT",FACE,{"disambiguationData":[TD([[makeQuery(id+"F12.imprint","IMPRINT",EDGE,{"derivedFrom":sQuery(id+"F12.wireOp",EDGE,"E66.MirrorCS")}),-1.0]])]});
            var Q7;
            Q7=makeQuery(id+"F12.imprint","IMPRINT",FACE,{"disambiguationData":[TD([[makeQuery(id+"F12.imprint","IMPRINT",EDGE,{"derivedFrom":sQuery(id+"F12.wireOp",EDGE,"E72.MirrorCS")}),-1.0]])]});
            var Q8;
            Q8=makeQuery(id+"F12.imprint","IMPRINT",FACE,{"disambiguationData":[TD([[makeQuery(id+"F12.imprint","IMPRINT",EDGE,{"derivedFrom":sQuery(id+"F12.wireOp",EDGE,"E71.MirrorCS")}),-1.0]])]});
            var Q9;
            Q9=makeQuery(id+"F12.imprint","IMPRINT",FACE,{"disambiguationData":[TD([[makeQuery(id+"F12.imprint","IMPRINT",EDGE,{"derivedFrom":sQuery(id+"F12.wireOp",EDGE,"E70.MirrorCS")}),1.0]])]});
            var Q10;
            Q10=makeQuery(id+"F12.imprint","IMPRINT",FACE,{"disambiguationData":[TD([[makeQuery(id+"F12.imprint","IMPRINT",EDGE,{"derivedFrom":sQuery(id+"F12.wireOp",EDGE,"E77.MirrorCS")}),-1.0]])]});
            var Q11;
            Q11=makeQuery(id+"F12.imprint","IMPRINT",FACE,{"disambiguationData":[TD([[makeQuery(id+"F12.imprint","IMPRINT",EDGE,{"derivedFrom":sQuery(id+"F12.wireOp",EDGE,"E82.MirrorCS")}),1.0]])]});
            extrude(context, id + "F13", {"entities" : qUnion([Q0, Q1, Q2, Q3, Q4, Q5, Q6, Q7, Q8, Q9, Q10, Q11]), "operationType" : NewBodyOperationType.REMOVE, "oppositeDirection" : true, "depth" : 25 * mm});
        }
        {
            var Q0;
            Q0=makeQuery(id+"F2.opExtrude","CAP_FACE",FACE,{"disambiguationData":[OSD([sQuery(id+"F1.wireOp",EDGE,"E0.bottom"),sQuery(id+"F1.wireOp",EDGE,"E0.top"),sQuery(id+"F1.wireOp",EDGE,"E0.left"),sQuery(id+"F1.wireOp",EDGE,"E0.right")])],"isStart":false});
            var sketch = newSketch(context, id + "F14", { "sketchPlane" : qUnion([Q0])});
            skLineSegment(sketch, "E92.bottom", {"start": v(-97, 92) * mm, "end": v(-92, 92) * mm});
            skLineSegment(sketch, "E92.top", {"start": v(-97, -92) * mm, "end": v(-92, -92) * mm});
            skLineSegment(sketch, "E92.left", {"start": v(-97, 92) * mm, "end": v(-97, -92) * mm});
            skLineSegment(sketch, "E92.right", {"start": v(-92, 92) * mm, "end": v(-92, -92) * mm});
            skSolve(sketch);
        }
        {
            var Q0;
            Q0=qSketchRegion(id+"F14",true);
            extrude(context, id + "F15", {"entities" : qUnion([Q0]), "depth" : 100 * mm});
        }
        {
            var Q0;
            Q0=makeQuery(id+"F9.imprint","IMPRINT",FACE,{"disambiguationData":[TD([[makeQuery(id+"F9.imprint","IMPRINT",EDGE,{"derivedFrom":sQuery(id+"F9.wireOp",EDGE,"E36.bottom")}),-1.0]])]});
            var Q1;
            Q1=makeQuery(id+"F9.imprint","IMPRINT",FACE,{"disambiguationData":[TD([[makeQuery(id+"F9.imprint","IMPRINT",EDGE,{"derivedFrom":sQuery(id+"F9.wireOp",EDGE,"E37.1.0.0")}),1.0]])]});
            var Q2;
            Q2=makeQuery(id+"F9.imprint","IMPRINT",FACE,{"disambiguationData":[TD([[makeQuery(id+"F9.imprint","IMPRINT",EDGE,{"derivedFrom":sQuery(id+"F9.wireOp",EDGE,"E37.2.0.0")}),1.0]])]});
            var Q3;
            Q3=makeQuery(id+"F9.imprint","IMPRINT",FACE,{"disambiguationData":[TD([[makeQuery(id+"F9.imprint","IMPRINT",EDGE,{"derivedFrom":sQuery(id+"F9.wireOp",EDGE,"E37.3.0.0")}),1.0]])]});
            var Q4;
            Q4=makeQuery(id+"F9.imprint","IMPRINT",FACE,{"disambiguationData":[TD([[makeQuery(id+"F9.imprint","IMPRINT",EDGE,{"derivedFrom":sQuery(id+"F9.wireOp",EDGE,"E37.4.0.0")}),1.0]])]});
            var Q5;
            Q5=makeQuery(id+"F9.imprint","IMPRINT",FACE,{"disambiguationData":[TD([[makeQuery(id+"F9.imprint","IMPRINT",EDGE,{"derivedFrom":sQuery(id+"F9.wireOp",EDGE,"E37.5.0.0")}),1.0]])]});
            var Q6;
            Q6=makeQuery(id+"F2.opExtrude","CAP_FACE",FACE,{"disambiguationData":[OSD([sQuery(id+"F1.wireOp",EDGE,"E0.bottom"),sQuery(id+"F1.wireOp",EDGE,"E0.top"),sQuery(id+"F1.wireOp",EDGE,"E0.left"),sQuery(id+"F1.wireOp",EDGE,"E0.right")])],"isStart":false});
            extrude(context, id + "F16", {"entities" : qUnion([Q0, Q1, Q2, Q3, Q4, Q5]), "endBound" : BoundingType.UP_TO_SURFACE, "oppositeDirection" : true, "endBoundEntityFace" : qUnion([Q6]), "depth" : 25 * mm});
        }
        {
            var Q0;
            Q0=makeQuery(id+"F15.opExtrude","SWEPT_BODY",BODY,{"disambiguationData":[OSD([sQuery(id+"F14.wireOp",EDGE,"E92.bottom"),sQuery(id+"F14.wireOp",EDGE,"E92.top"),sQuery(id+"F14.wireOp",EDGE,"E92.left"),sQuery(id+"F14.wireOp",EDGE,"E92.right")])]});
            var Q1;
            Q1=makeQuery(id+"F16.opExtrude","SWEPT_BODY",BODY,{"disambiguationData":[OSD([sQuery(id+"F9.wireOp",EDGE,"E37.5.0.0"),sQuery(id+"F9.wireOp",EDGE,"E37.5.0.1"),sQuery(id+"F9.wireOp",EDGE,"E37.5.0.2"),sQuery(id+"F9.wireOp",EDGE,"E37.5.0.3")])]});
            var Q2;
            Q2=makeQuery(id+"F16.opExtrude","SWEPT_BODY",BODY,{"disambiguationData":[OSD([sQuery(id+"F9.wireOp",EDGE,"E37.4.0.0"),sQuery(id+"F9.wireOp",EDGE,"E37.4.0.1"),sQuery(id+"F9.wireOp",EDGE,"E37.4.0.2"),sQuery(id+"F9.wireOp",EDGE,"E37.4.0.3")])]});
            var Q3;
            Q3=makeQuery(id+"F16.opExtrude","SWEPT_BODY",BODY,{"disambiguationData":[OSD([sQuery(id+"F9.wireOp",EDGE,"E37.3.0.0"),sQuery(id+"F9.wireOp",EDGE,"E37.3.0.1"),sQuery(id+"F9.wireOp",EDGE,"E37.3.0.2"),sQuery(id+"F9.wireOp",EDGE,"E37.3.0.3")])]});
            var Q4;
            Q4=makeQuery(id+"F16.opExtrude","SWEPT_BODY",BODY,{"disambiguationData":[OSD([sQuery(id+"F9.wireOp",EDGE,"E37.2.0.0"),sQuery(id+"F9.wireOp",EDGE,"E37.2.0.1"),sQuery(id+"F9.wireOp",EDGE,"E37.2.0.2"),sQuery(id+"F9.wireOp",EDGE,"E37.2.0.3")])]});
            var Q5;
            Q5=makeQuery(id+"F16.opExtrude","SWEPT_BODY",BODY,{"disambiguationData":[OSD([sQuery(id+"F9.wireOp",EDGE,"E37.1.0.0"),sQuery(id+"F9.wireOp",EDGE,"E37.1.0.1"),sQuery(id+"F9.wireOp",EDGE,"E37.1.0.2"),sQuery(id+"F9.wireOp",EDGE,"E37.1.0.3")])]});
            var Q6;
            Q6=makeQuery(id+"F16.opExtrude","SWEPT_BODY",BODY,{"disambiguationData":[OSD([sQuery(id+"F9.wireOp",EDGE,"E36.bottom"),sQuery(id+"F9.wireOp",EDGE,"E36.top"),sQuery(id+"F9.wireOp",EDGE,"E36.left"),sQuery(id+"F9.wireOp",EDGE,"E36.right")])]});
            booleanBodies(context, id + "F17", {"operationType" : BooleanOperationType.UNION, "tools" : qUnion([Q0, Q1, Q2, Q3, Q4, Q5, Q6])});
        }
        {
            var Q0;
            Q0=makeQuery(id+"F8.opExtrude","SWEPT_BODY",BODY,{"disambiguationData":[OSD([sQuery(id+"F7.wireOp",EDGE,"E34.bottom"),sQuery(id+"F7.wireOp",EDGE,"E34.top"),sQuery(id+"F7.wireOp",EDGE,"E34.left"),sQuery(id+"F7.wireOp",EDGE,"E34.right")])]});
            transform(context, id + "F18", {"entities" : qUnion([Q0]), "transformType" : TransformType.TRANSLATION_3D, "dx" : 0 * mm, "dy" : -189 * mm, "dz" : 0 * mm, "makeCopy" : true});
        }
        {
            var Q0;
            Q0=makeQuery(id+"F11.opBoolean","MERGE",FACE,{"derivedFrom":[makeQuery(id+"F6.opExtrude","SWEPT_FACE",FACE,{"disambiguationData":[OSD([sQuery(id+"F3.wireOp",EDGE,"E4.top")])]}),makeQuery(id+"F6.opExtrude","SWEPT_FACE",FACE,{"disambiguationData":[OSD([sQuery(id+"F3.wireOp",EDGE,"E5.1.0.1")])]}),makeQuery(id+"F6.opExtrude","SWEPT_FACE",FACE,{"disambiguationData":[OSD([sQuery(id+"F3.wireOp",EDGE,"E5.2.0.1")])]}),makeQuery(id+"F6.opExtrude","SWEPT_FACE",FACE,{"disambiguationData":[OSD([sQuery(id+"F3.wireOp",EDGE,"E5.3.0.1")])]}),makeQuery(id+"F6.opExtrude","SWEPT_FACE",FACE,{"disambiguationData":[OSD([sQuery(id+"F3.wireOp",EDGE,"E5.4.0.1")])]}),makeQuery(id+"F6.opExtrude","SWEPT_FACE",FACE,{"disambiguationData":[OSD([sQuery(id+"F3.wireOp",EDGE,"E5.5.0.1")])]}),makeQuery(id+"F8.opExtrude","SWEPT_FACE",FACE,{"disambiguationData":[OSD([sQuery(id+"F7.wireOp",EDGE,"E34.top")])]})]});
            var sketch = newSketch(context, id + "F19", { "sketchPlane" : qUnion([Q0])});
            skLineSegment(sketch, "E93", {"start": v(-97, 105) * mm, "end": v(-92, 105) * mm});
            skLineSegment(sketch, "E94", {"start": v(-97, 5) * mm, "end": v(-92, 5) * mm});
            skPoint(sketch, "E95", {"position": v(-97, 103.5) * mm});
            skLineSegment(sketch, "E96.bottom", {"start": v(-97, 103.5) * mm, "end": v(-92, 103.5) * mm});
            skLineSegment(sketch, "E96.top", {"start": v(-97, 94.65) * mm, "end": v(-92, 94.65) * mm});
            skLineSegment(sketch, "E96.left", {"start": v(-97, 103.5) * mm, "end": v(-97, 94.65) * mm});
            skLineSegment(sketch, "E96.right", {"start": v(-92, 103.5) * mm, "end": v(-92, 94.65) * mm});
            skLineSegment(sketch, "E97.1.0.0", {"start": v(-97, 77.02) * mm, "end": v(-92, 77.02) * mm});
            skLineSegment(sketch, "E97.1.0.1", {"start": v(-97, 85.87) * mm, "end": v(-97, 77.02) * mm});
            skLineSegment(sketch, "E97.1.0.2", {"start": v(-97, 85.87) * mm, "end": v(-92, 85.87) * mm});
            skLineSegment(sketch, "E97.1.0.3", {"start": v(-92, 85.87) * mm, "end": v(-92, 77.02) * mm});
            skLineSegment(sketch, "E97.2.0.0", {"start": v(-97, 59.4) * mm, "end": v(-92, 59.4) * mm});
            skLineSegment(sketch, "E97.2.0.1", {"start": v(-97, 68.24) * mm, "end": v(-97, 59.4) * mm});
            skLineSegment(sketch, "E97.2.0.2", {"start": v(-97, 68.24) * mm, "end": v(-92, 68.24) * mm});
            skLineSegment(sketch, "E97.2.0.3", {"start": v(-92, 68.24) * mm, "end": v(-92, 59.4) * mm});
            skLineSegment(sketch, "E97.3.0.0", {"start": v(-97, 41.76) * mm, "end": v(-92, 41.76) * mm});
            skLineSegment(sketch, "E97.3.0.1", {"start": v(-97, 50.6) * mm, "end": v(-97, 41.76) * mm});
            skLineSegment(sketch, "E97.3.0.2", {"start": v(-97, 50.6) * mm, "end": v(-92, 50.6) * mm});
            skLineSegment(sketch, "E97.3.0.3", {"start": v(-92, 50.6) * mm, "end": v(-92, 41.76) * mm});
            skLineSegment(sketch, "E97.4.0.0", {"start": v(-97, 24.13) * mm, "end": v(-92, 24.13) * mm});
            skLineSegment(sketch, "E97.4.0.1", {"start": v(-97, 32.98) * mm, "end": v(-97, 24.13) * mm});
            skLineSegment(sketch, "E97.4.0.2", {"start": v(-97, 32.98) * mm, "end": v(-92, 32.98) * mm});
            skLineSegment(sketch, "E97.4.0.3", {"start": v(-92, 32.98) * mm, "end": v(-92, 24.13) * mm});
            skLineSegment(sketch, "E97.5.0.0", {"start": v(-97, 6.5) * mm, "end": v(-92, 6.5) * mm});
            skLineSegment(sketch, "E97.5.0.1", {"start": v(-97, 15.35) * mm, "end": v(-97, 6.5) * mm});
            skLineSegment(sketch, "E97.5.0.2", {"start": v(-97, 15.35) * mm, "end": v(-92, 15.35) * mm});
            skLineSegment(sketch, "E97.5.0.3", {"start": v(-92, 15.35) * mm, "end": v(-92, 6.5) * mm});
            skLineSegment(sketch, "E97.direction1", {"start": v(-97, 94.65) * mm, "end": v(-97, 77.02) * mm, "construction": true});
            skSolve(sketch);
        }
        {
            var Q0;
            Q0=makeQuery(id+"F19.imprint","IMPRINT",FACE,{"disambiguationData":[TD([[makeQuery(id+"F19.imprint","IMPRINT",EDGE,{"derivedFrom":sQuery(id+"F19.wireOp",EDGE,"E96.bottom")}),-1.0]])]});
            var Q1;
            Q1=makeQuery(id+"F19.imprint","IMPRINT",FACE,{"disambiguationData":[TD([[makeQuery(id+"F19.imprint","IMPRINT",EDGE,{"derivedFrom":sQuery(id+"F19.wireOp",EDGE,"E97.1.0.0")}),1.0]])]});
            var Q2;
            Q2=makeQuery(id+"F19.imprint","IMPRINT",FACE,{"disambiguationData":[TD([[makeQuery(id+"F19.imprint","IMPRINT",EDGE,{"derivedFrom":sQuery(id+"F19.wireOp",EDGE,"E97.2.0.0")}),1.0]])]});
            var Q3;
            Q3=makeQuery(id+"F19.imprint","IMPRINT",FACE,{"disambiguationData":[TD([[makeQuery(id+"F19.imprint","IMPRINT",EDGE,{"derivedFrom":sQuery(id+"F19.wireOp",EDGE,"E97.3.0.0")}),1.0]])]});
            var Q4;
            Q4=makeQuery(id+"F19.imprint","IMPRINT",FACE,{"disambiguationData":[TD([[makeQuery(id+"F19.imprint","IMPRINT",EDGE,{"derivedFrom":sQuery(id+"F19.wireOp",EDGE,"E97.4.0.0")}),1.0]])]});
            var Q5;
            Q5=makeQuery(id+"F19.imprint","IMPRINT",FACE,{"disambiguationData":[TD([[makeQuery(id+"F19.imprint","IMPRINT",EDGE,{"derivedFrom":sQuery(id+"F19.wireOp",EDGE,"E97.5.0.0")}),1.0]])]});
            extrude(context, id + "F20", {"entities" : qUnion([Q0, Q1, Q2, Q3, Q4, Q5]), "operationType" : NewBodyOperationType.REMOVE, "oppositeDirection" : true, "depth" : 25 * mm, "offsetDistance" : 25 * mm});
        }
        {
            var Q0;
            Q0=qSketchRegion(id+"F19",true);
            var Q1;
            Q1=makeQuery(id+"F11.opBoolean","MERGE",FACE,{"derivedFrom":[makeQuery(id+"F6.opExtrude","SWEPT_FACE",FACE,{"disambiguationData":[OSD([sQuery(id+"F5.wireOp",EDGE,"E33.0")])]}),makeQuery(id+"F6.opExtrude","SWEPT_FACE",FACE,{"disambiguationData":[OSD([sQuery(id+"F3.wireOp",EDGE,"E5.1.0.2")])]}),makeQuery(id+"F6.opExtrude","SWEPT_FACE",FACE,{"disambiguationData":[OSD([sQuery(id+"F3.wireOp",EDGE,"E5.2.0.2")])]}),makeQuery(id+"F6.opExtrude","SWEPT_FACE",FACE,{"disambiguationData":[OSD([sQuery(id+"F3.wireOp",EDGE,"E5.3.0.2")])]}),makeQuery(id+"F6.opExtrude","SWEPT_FACE",FACE,{"disambiguationData":[OSD([sQuery(id+"F3.wireOp",EDGE,"E5.4.0.2")])]}),makeQuery(id+"F6.opExtrude","SWEPT_FACE",FACE,{"disambiguationData":[OSD([sQuery(id+"F3.wireOp",EDGE,"E5.5.0.2")])]}),makeQuery(id+"F8.opExtrude","SWEPT_FACE",FACE,{"disambiguationData":[OSD([sQuery(id+"F7.wireOp",EDGE,"E34.bottom")])]})]});
            extrude(context, id + "F21", {"entities" : qUnion([Q0]), "endBound" : BoundingType.UP_TO_SURFACE, "oppositeDirection" : true, "depth" : 25 * mm, "endBoundEntityFace" : qUnion([Q1]), "offsetDistance" : 25 * mm});
        }
        {
            var Q0;
            Q0=makeQuery(id+"F15.opExtrude","SWEPT_BODY",BODY,{"disambiguationData":[OSD([sQuery(id+"F14.wireOp",EDGE,"E92.bottom"),sQuery(id+"F14.wireOp",EDGE,"E92.top"),sQuery(id+"F14.wireOp",EDGE,"E92.left"),sQuery(id+"F14.wireOp",EDGE,"E92.right")])]});
            var Q1;
            Q1=makeQuery(id+"F21.opExtrude","SWEPT_BODY",BODY,{"disambiguationData":[OSD([sQuery(id+"F19.wireOp",EDGE,"E96.bottom"),sQuery(id+"F19.wireOp",EDGE,"E96.top"),sQuery(id+"F19.wireOp",EDGE,"E96.left"),sQuery(id+"F19.wireOp",EDGE,"E96.right")])]});
            var Q2;
            Q2=makeQuery(id+"F21.opExtrude","SWEPT_BODY",BODY,{"disambiguationData":[OSD([sQuery(id+"F19.wireOp",EDGE,"E97.1.0.0"),sQuery(id+"F19.wireOp",EDGE,"E97.1.0.1"),sQuery(id+"F19.wireOp",EDGE,"E97.1.0.2"),sQuery(id+"F19.wireOp",EDGE,"E97.1.0.3")])]});
            var Q3;
            Q3=makeQuery(id+"F21.opExtrude","SWEPT_BODY",BODY,{"disambiguationData":[OSD([sQuery(id+"F19.wireOp",EDGE,"E97.2.0.0"),sQuery(id+"F19.wireOp",EDGE,"E97.2.0.1"),sQuery(id+"F19.wireOp",EDGE,"E97.2.0.2"),sQuery(id+"F19.wireOp",EDGE,"E97.2.0.3")])]});
            var Q4;
            Q4=makeQuery(id+"F21.opExtrude","SWEPT_BODY",BODY,{"disambiguationData":[OSD([sQuery(id+"F19.wireOp",EDGE,"E97.3.0.0"),sQuery(id+"F19.wireOp",EDGE,"E97.3.0.1"),sQuery(id+"F19.wireOp",EDGE,"E97.3.0.2"),sQuery(id+"F19.wireOp",EDGE,"E97.3.0.3")])]});
            var Q5;
            Q5=makeQuery(id+"F21.opExtrude","SWEPT_BODY",BODY,{"disambiguationData":[OSD([sQuery(id+"F19.wireOp",EDGE,"E97.4.0.0"),sQuery(id+"F19.wireOp",EDGE,"E97.4.0.1"),sQuery(id+"F19.wireOp",EDGE,"E97.4.0.2"),sQuery(id+"F19.wireOp",EDGE,"E97.4.0.3")])]});
            var Q6;
            Q6=makeQuery(id+"F21.opExtrude","SWEPT_BODY",BODY,{"disambiguationData":[OSD([sQuery(id+"F19.wireOp",EDGE,"E97.5.0.0"),sQuery(id+"F19.wireOp",EDGE,"E97.5.0.1"),sQuery(id+"F19.wireOp",EDGE,"E97.5.0.2"),sQuery(id+"F19.wireOp",EDGE,"E97.5.0.3")])]});
            booleanBodies(context, id + "F22", {"operationType" : BooleanOperationType.UNION, "tools" : qUnion([Q0, Q1, Q2, Q3, Q4, Q5, Q6])});
        }
        {
            var Q0;
            {var subQ35=sQuery(id+"F19.wireOp",EDGE,"E93");Q0=makeQuery(id+"F19.imprint","IMPRINT",FACE,{"disambiguationData":[TD([[makeQuery(id+"F19.imprint","IMPRINT",EDGE,{"derivedFrom":subQ35}),-1.0]])]});}
            var sketch = newSketch(context, id + "F23", { "sketchPlane" : qUnion([Q0])});
            skLineSegment(sketch, "E98.MirrorCS", {"start": v(92, 94.65) * mm, "end": v(92, 103.5) * mm});
            skLineSegment(sketch, "E99.MirrorCS", {"start": v(92, 103.5) * mm, "end": v(97, 103.5) * mm});
            skLineSegment(sketch, "E100.MirrorCS", {"start": v(97, 103.5) * mm, "end": v(97, 94.65) * mm});
            skLineSegment(sketch, "E101.MirrorCS", {"start": v(97, 94.65) * mm, "end": v(92, 94.65) * mm});
            skLineSegment(sketch, "E102.MirrorCS", {"start": v(97, 77.02) * mm, "end": v(92, 77.02) * mm});
            skLineSegment(sketch, "E103.MirrorCS", {"start": v(97, 85.87) * mm, "end": v(97, 77.02) * mm});
            skLineSegment(sketch, "E104.MirrorCS", {"start": v(92, 77.02) * mm, "end": v(92, 85.87) * mm});
            skLineSegment(sketch, "E105.MirrorCS", {"start": v(92, 85.87) * mm, "end": v(97, 85.87) * mm});
            skLineSegment(sketch, "E106.MirrorCS", {"start": v(92, 32.98) * mm, "end": v(97, 32.98) * mm});
            skLineSegment(sketch, "E107.MirrorCS", {"start": v(92, 68.24) * mm, "end": v(97, 68.24) * mm});
            skLineSegment(sketch, "E108.MirrorCS", {"start": v(97, 6.5) * mm, "end": v(92, 6.5) * mm});
            skLineSegment(sketch, "E109.MirrorCS", {"start": v(92, 15.35) * mm, "end": v(97, 15.35) * mm});
            skLineSegment(sketch, "E110.MirrorCS", {"start": v(97, 59.4) * mm, "end": v(92, 59.4) * mm});
            skLineSegment(sketch, "E111.MirrorCS", {"start": v(97, 41.76) * mm, "end": v(92, 41.76) * mm});
            skLineSegment(sketch, "E112.MirrorCS", {"start": v(97, 24.13) * mm, "end": v(92, 24.13) * mm});
            skLineSegment(sketch, "E113.MirrorCS", {"start": v(92, 50.6) * mm, "end": v(97, 50.6) * mm});
            skLineSegment(sketch, "E114.MirrorCS", {"start": v(92, 59.4) * mm, "end": v(92, 68.24) * mm});
            skLineSegment(sketch, "E115.MirrorCS", {"start": v(92, 41.76) * mm, "end": v(92, 50.6) * mm});
            skLineSegment(sketch, "E116.MirrorCS", {"start": v(92, 24.13) * mm, "end": v(92, 32.98) * mm});
            skLineSegment(sketch, "E117.MirrorCS", {"start": v(97, 50.6) * mm, "end": v(97, 41.76) * mm});
            skLineSegment(sketch, "E118.MirrorCS", {"start": v(92, 6.5) * mm, "end": v(92, 15.35) * mm});
            skLineSegment(sketch, "E119.MirrorCS", {"start": v(97, 15.35) * mm, "end": v(97, 6.5) * mm});
            skLineSegment(sketch, "E120.MirrorCS", {"start": v(97, 68.24) * mm, "end": v(97, 59.4) * mm});
            skLineSegment(sketch, "E121.MirrorCS", {"start": v(97, 32.98) * mm, "end": v(97, 24.13) * mm});
            skSolve(sketch);
        }
        {
            var Q0;
            Q0=qSketchRegion(id+"F23",true);
            extrude(context, id + "F24", {"entities" : qUnion([Q0]), "operationType" : NewBodyOperationType.REMOVE, "oppositeDirection" : true, "depth" : 25 * mm, "offsetDistance" : 25 * mm});
        }
        {
            var Q0;
            Q0=makeQuery(id+"F18.opPattern","COPY",FACE,{"derivedFrom":makeQuery(id+"F11.opBoolean","MERGE",FACE,{"derivedFrom":[makeQuery(id+"F6.opExtrude","SWEPT_FACE",FACE,{"disambiguationData":[OSD([sQuery(id+"F5.wireOp",EDGE,"E33.0")])]}),makeQuery(id+"F6.opExtrude","SWEPT_FACE",FACE,{"disambiguationData":[OSD([sQuery(id+"F3.wireOp",EDGE,"E5.1.0.2")])]}),makeQuery(id+"F6.opExtrude","SWEPT_FACE",FACE,{"disambiguationData":[OSD([sQuery(id+"F3.wireOp",EDGE,"E5.2.0.2")])]}),makeQuery(id+"F6.opExtrude","SWEPT_FACE",FACE,{"disambiguationData":[OSD([sQuery(id+"F3.wireOp",EDGE,"E5.3.0.2")])]}),makeQuery(id+"F6.opExtrude","SWEPT_FACE",FACE,{"disambiguationData":[OSD([sQuery(id+"F3.wireOp",EDGE,"E5.4.0.2")])]}),makeQuery(id+"F6.opExtrude","SWEPT_FACE",FACE,{"disambiguationData":[OSD([sQuery(id+"F3.wireOp",EDGE,"E5.5.0.2")])]}),makeQuery(id+"F8.opExtrude","SWEPT_FACE",FACE,{"disambiguationData":[OSD([sQuery(id+"F7.wireOp",EDGE,"E34.bottom")])]})]}),"instanceName":"1"});
            var sketch = newSketch(context, id + "F25", { "sketchPlane" : qUnion([Q0])});
            skLineSegment(sketch, "E122.0", {"start": v(97, 105) * mm, "end": v(92, 105) * mm});
            skLineSegment(sketch, "E123", {"start": v(97, 5) * mm, "end": v(92, 5) * mm});
            skPoint(sketch, "E124", {"position": v(91.95, 103.5) * mm});
            skLineSegment(sketch, "E125.bottom", {"start": v(91.95, 103.5) * mm, "end": v(96.95, 103.5) * mm});
            skLineSegment(sketch, "E125.top", {"start": v(91.95, 94.66) * mm, "end": v(96.95, 94.66) * mm});
            skLineSegment(sketch, "E125.left", {"start": v(91.95, 103.5) * mm, "end": v(91.95, 94.66) * mm});
            skLineSegment(sketch, "E125.right", {"start": v(96.95, 103.5) * mm, "end": v(96.95, 94.66) * mm});
            skLineSegment(sketch, "E126.1.0.0", {"start": v(91.95, 85.87) * mm, "end": v(96.95, 85.87) * mm});
            skLineSegment(sketch, "E126.1.0.1", {"start": v(96.95, 85.87) * mm, "end": v(96.95, 77.02) * mm});
            skLineSegment(sketch, "E126.1.0.2", {"start": v(91.95, 85.87) * mm, "end": v(91.95, 77.02) * mm});
            skLineSegment(sketch, "E126.1.0.3", {"start": v(91.95, 77.02) * mm, "end": v(96.95, 77.02) * mm});
            skLineSegment(sketch, "E126.2.0.0", {"start": v(91.95, 68.24) * mm, "end": v(96.95, 68.24) * mm});
            skLineSegment(sketch, "E126.2.0.1", {"start": v(96.95, 68.24) * mm, "end": v(96.95, 59.4) * mm});
            skLineSegment(sketch, "E126.2.0.2", {"start": v(91.95, 68.24) * mm, "end": v(91.95, 59.4) * mm});
            skLineSegment(sketch, "E126.2.0.3", {"start": v(91.95, 59.4) * mm, "end": v(96.95, 59.4) * mm});
            skLineSegment(sketch, "E126.3.0.0", {"start": v(91.95, 50.6) * mm, "end": v(96.95, 50.6) * mm});
            skLineSegment(sketch, "E126.3.0.1", {"start": v(96.95, 50.6) * mm, "end": v(96.95, 41.76) * mm});
            skLineSegment(sketch, "E126.3.0.2", {"start": v(91.95, 50.6) * mm, "end": v(91.95, 41.76) * mm});
            skLineSegment(sketch, "E126.3.0.3", {"start": v(91.95, 41.76) * mm, "end": v(96.95, 41.76) * mm});
            skLineSegment(sketch, "E126.4.0.0", {"start": v(91.95, 32.98) * mm, "end": v(96.95, 32.98) * mm});
            skLineSegment(sketch, "E126.4.0.1", {"start": v(96.95, 32.98) * mm, "end": v(96.95, 24.13) * mm});
            skLineSegment(sketch, "E126.4.0.2", {"start": v(91.95, 32.98) * mm, "end": v(91.95, 24.13) * mm});
            skLineSegment(sketch, "E126.4.0.3", {"start": v(91.95, 24.13) * mm, "end": v(96.95, 24.13) * mm});
            skLineSegment(sketch, "E126.5.0.0", {"start": v(91.95, 15.35) * mm, "end": v(96.95, 15.35) * mm});
            skLineSegment(sketch, "E126.5.0.1", {"start": v(96.95, 15.35) * mm, "end": v(96.95, 6.5) * mm});
            skLineSegment(sketch, "E126.5.0.2", {"start": v(91.95, 15.35) * mm, "end": v(91.95, 6.5) * mm});
            skLineSegment(sketch, "E126.5.0.3", {"start": v(91.95, 6.5) * mm, "end": v(96.95, 6.5) * mm});
            skLineSegment(sketch, "E126.direction1", {"start": v(91.95, 103.5) * mm, "end": v(91.95, 85.87) * mm, "construction": true});
            skSolve(sketch);
        }
        {
            var Q0;
            Q0=makeQuery(id+"F25.imprint","IMPRINT",FACE,{"disambiguationData":[TD([[makeQuery(id+"F25.imprint","IMPRINT",EDGE,{"derivedFrom":sQuery(id+"F25.wireOp",EDGE,"E125.bottom")}),-1.0]])]});
            var Q1;
            Q1=makeQuery(id+"F25.imprint","IMPRINT",FACE,{"disambiguationData":[TD([[makeQuery(id+"F25.imprint","IMPRINT",EDGE,{"derivedFrom":sQuery(id+"F25.wireOp",EDGE,"E126.1.0.0")}),-1.0]])]});
            var Q2;
            Q2=makeQuery(id+"F25.imprint","IMPRINT",FACE,{"disambiguationData":[TD([[makeQuery(id+"F25.imprint","IMPRINT",EDGE,{"derivedFrom":sQuery(id+"F25.wireOp",EDGE,"E126.2.0.0")}),-1.0]])]});
            var Q3;
            Q3=makeQuery(id+"F25.imprint","IMPRINT",FACE,{"disambiguationData":[TD([[makeQuery(id+"F25.imprint","IMPRINT",EDGE,{"derivedFrom":sQuery(id+"F25.wireOp",EDGE,"E126.3.0.0")}),-1.0]])]});
            var Q4;
            Q4=makeQuery(id+"F25.imprint","IMPRINT",FACE,{"disambiguationData":[TD([[makeQuery(id+"F25.imprint","IMPRINT",EDGE,{"derivedFrom":sQuery(id+"F25.wireOp",EDGE,"E126.4.0.0")}),-1.0]])]});
            var Q5;
            Q5=makeQuery(id+"F25.imprint","IMPRINT",FACE,{"disambiguationData":[TD([[makeQuery(id+"F25.imprint","IMPRINT",EDGE,{"derivedFrom":sQuery(id+"F25.wireOp",EDGE,"E126.5.0.0")}),-1.0]])]});
            extrude(context, id + "F26", {"entities" : qUnion([Q0, Q1, Q2, Q3, Q4, Q5]), "operationType" : NewBodyOperationType.REMOVE, "oppositeDirection" : true, "depth" : 25 * mm, "offsetDistance" : 25 * mm});
        }
        {
            var Q0;
            Q0=makeQuery(id+"F25.imprint","IMPRINT",FACE,{"disambiguationData":[TD([[makeQuery(id+"F25.imprint","IMPRINT",EDGE,{"derivedFrom":sQuery(id+"F25.wireOp",EDGE,"E125.bottom")}),-1.0]])]});
            var Q1;
            Q1=makeQuery(id+"F25.imprint","IMPRINT",FACE,{"disambiguationData":[TD([[makeQuery(id+"F25.imprint","IMPRINT",EDGE,{"derivedFrom":sQuery(id+"F25.wireOp",EDGE,"E126.1.0.0")}),-1.0]])]});
            var Q2;
            Q2=makeQuery(id+"F25.imprint","IMPRINT",FACE,{"disambiguationData":[TD([[makeQuery(id+"F25.imprint","IMPRINT",EDGE,{"derivedFrom":sQuery(id+"F25.wireOp",EDGE,"E126.2.0.0")}),-1.0]])]});
            var Q3;
            Q3=makeQuery(id+"F25.imprint","IMPRINT",FACE,{"disambiguationData":[TD([[makeQuery(id+"F25.imprint","IMPRINT",EDGE,{"derivedFrom":sQuery(id+"F25.wireOp",EDGE,"E126.3.0.0")}),-1.0]])]});
            var Q4;
            Q4=makeQuery(id+"F25.imprint","IMPRINT",FACE,{"disambiguationData":[TD([[makeQuery(id+"F25.imprint","IMPRINT",EDGE,{"derivedFrom":sQuery(id+"F25.wireOp",EDGE,"E126.4.0.0")}),-1.0]])]});
            var Q5;
            Q5=makeQuery(id+"F25.imprint","IMPRINT",FACE,{"disambiguationData":[TD([[makeQuery(id+"F25.imprint","IMPRINT",EDGE,{"derivedFrom":sQuery(id+"F25.wireOp",EDGE,"E126.5.0.0")}),-1.0]])]});
            var Q6;
            Q6=makeQuery(id+"F18.opPattern","COPY",FACE,{"derivedFrom":makeQuery(id+"F11.opBoolean","MERGE",FACE,{"derivedFrom":[makeQuery(id+"F6.opExtrude","SWEPT_FACE",FACE,{"disambiguationData":[OSD([sQuery(id+"F3.wireOp",EDGE,"E4.top")])]}),makeQuery(id+"F6.opExtrude","SWEPT_FACE",FACE,{"disambiguationData":[OSD([sQuery(id+"F3.wireOp",EDGE,"E5.1.0.1")])]}),makeQuery(id+"F6.opExtrude","SWEPT_FACE",FACE,{"disambiguationData":[OSD([sQuery(id+"F3.wireOp",EDGE,"E5.2.0.1")])]}),makeQuery(id+"F6.opExtrude","SWEPT_FACE",FACE,{"disambiguationData":[OSD([sQuery(id+"F3.wireOp",EDGE,"E5.3.0.1")])]}),makeQuery(id+"F6.opExtrude","SWEPT_FACE",FACE,{"disambiguationData":[OSD([sQuery(id+"F3.wireOp",EDGE,"E5.4.0.1")])]}),makeQuery(id+"F6.opExtrude","SWEPT_FACE",FACE,{"disambiguationData":[OSD([sQuery(id+"F3.wireOp",EDGE,"E5.5.0.1")])]}),makeQuery(id+"F8.opExtrude","SWEPT_FACE",FACE,{"disambiguationData":[OSD([sQuery(id+"F7.wireOp",EDGE,"E34.top")])]})]}),"instanceName":"1"});
            extrude(context, id + "F27", {"entities" : qUnion([Q0, Q1, Q2, Q3, Q4, Q5]), "endBound" : BoundingType.UP_TO_SURFACE, "oppositeDirection" : true, "depth" : 25 * mm, "endBoundEntityFace" : qUnion([Q6]), "offsetDistance" : 25 * mm});
        }
        {
            var Q0;
            Q0=makeQuery(id+"F2.opExtrude","CAP_FACE",FACE,{"disambiguationData":[OSD([sQuery(id+"F1.wireOp",EDGE,"E0.bottom"),sQuery(id+"F1.wireOp",EDGE,"E0.top"),sQuery(id+"F1.wireOp",EDGE,"E0.left"),sQuery(id+"F1.wireOp",EDGE,"E0.right")])],"isStart":false});
            var sketch = newSketch(context, id + "F28", { "sketchPlane" : qUnion([Q0])});
            skLineSegment(sketch, "E127.bottom", {"start": v(-37.62, -42.22) * mm, "end": v(-71.5, -42.22) * mm});
            skLineSegment(sketch, "E127.top", {"start": v(-37.62, 42.22) * mm, "end": v(-71.5, 42.22) * mm});
            skLineSegment(sketch, "E127.left", {"start": v(-37.62, -42.22) * mm, "end": v(-37.62, 42.22) * mm});
            skLineSegment(sketch, "E127.right", {"start": v(-71.5, -42.22) * mm, "end": v(-71.5, 42.22) * mm});
            skPoint(sketch, "E127.middle", {"position": v(-54.56, 0) * mm});
            skLineSegment(sketch, "E128.MirrorCS", {"start": v(37.62, -42.22) * mm, "end": v(37.62, 42.22) * mm});
            skLineSegment(sketch, "E129.MirrorCS", {"start": v(37.62, 42.22) * mm, "end": v(71.5, 42.22) * mm});
            skLineSegment(sketch, "E130.MirrorCS", {"start": v(71.5, -42.22) * mm, "end": v(71.5, 42.22) * mm});
            skLineSegment(sketch, "E131.MirrorCS", {"start": v(37.62, -42.22) * mm, "end": v(71.5, -42.22) * mm});
            skSolve(sketch);
        }
        {
            var Q0;
            Q0=makeQuery(id+"F28.imprint","IMPRINT",FACE,{"disambiguationData":[TD([[makeQuery(id+"F28.imprint","IMPRINT",EDGE,{"derivedFrom":sQuery(id+"F28.wireOp",EDGE,"E127.bottom")}),-1.0]])]});
            var Q1;
            Q1=makeQuery(id+"F28.imprint","IMPRINT",FACE,{"disambiguationData":[TD([[makeQuery(id+"F28.imprint","IMPRINT",EDGE,{"derivedFrom":sQuery(id+"F28.wireOp",EDGE,"E129.MirrorCS")}),-1.0]])]});
            extrude(context, id + "F29", {"entities" : qUnion([Q0, Q1]), "operationType" : NewBodyOperationType.REMOVE, "oppositeDirection" : true, "depth" : 25 * mm, "offsetDistance" : 25 * mm});
        }
        {
            var Q0;
            Q0=makeQuery(id+"F15.opExtrude","CAP_FACE",FACE,{"disambiguationData":[OSD([sQuery(id+"F14.wireOp",EDGE,"E92.bottom"),sQuery(id+"F14.wireOp",EDGE,"E92.top"),sQuery(id+"F14.wireOp",EDGE,"E92.left"),sQuery(id+"F14.wireOp",EDGE,"E92.right")])],"isStart":false});
            cPlane(context, id + "F30", {"entities" : qUnion([Q0]), "cplaneType" : CPlaneType.OFFSET, "offset" : 50 * mm, "oppositeDirection" : true, "width" : 150 * mm, "height" : 150 * mm});
        }
        {
            var Q0;
            Q0=makeQuery(id+"F15.opExtrude","SWEPT_BODY",BODY,{"disambiguationData":[OSD([sQuery(id+"F14.wireOp",EDGE,"E92.bottom"),sQuery(id+"F14.wireOp",EDGE,"E92.top"),sQuery(id+"F14.wireOp",EDGE,"E92.left"),sQuery(id+"F14.wireOp",EDGE,"E92.right")])]});
            var Q1;
            Q1=qCreatedBy(id+"F30.planeOp",FACE);
            mirror(context, id + "F31", {"entities" : qUnion([Q0]), "mirrorPlane" : qUnion([Q1])});
        }
    });
